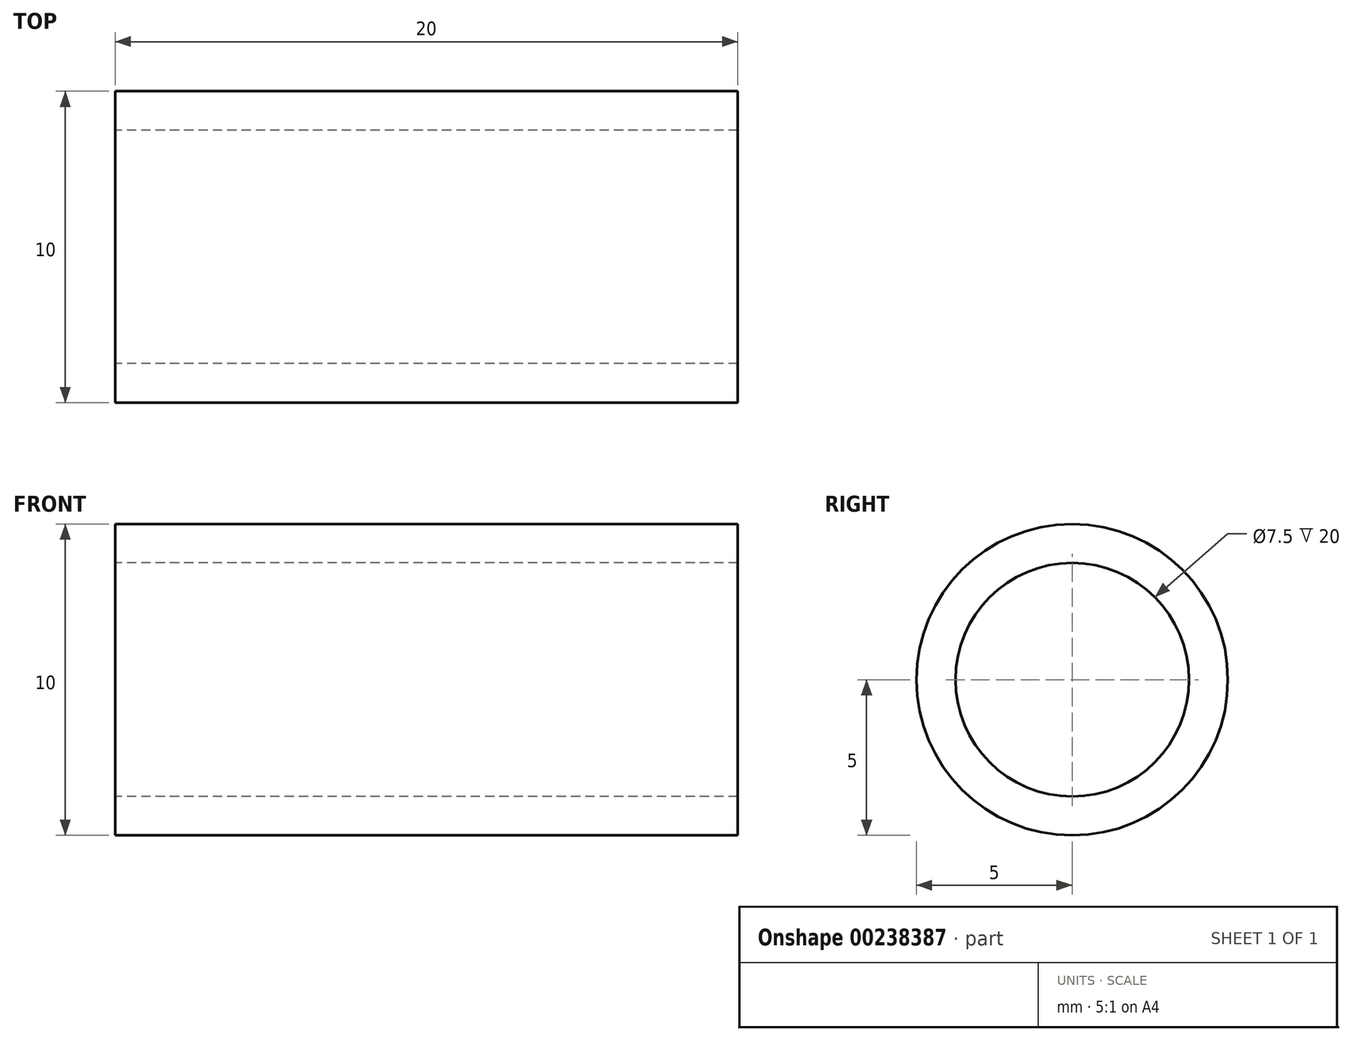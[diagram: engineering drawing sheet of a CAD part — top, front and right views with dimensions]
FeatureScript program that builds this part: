
annotation { "Feature Type Name" : "Feature", "Feature Type Description" : "" }
export const myFeature = defineFeature(function(context is Context, id is Id, definition is map)
    precondition{}
    {
        {
            var Q0;
            Q0=qCreatedBy(makeId("Right.planeOp"),FACE);
            var sketch = newSketch(context, id + "F0", { "sketchPlane" : qUnion([Q0])});
            skCircle(sketch, "E0", {"center": v(0, 0) * mm, "radius": 5 * mm});
            skCircle(sketch, "E1", {"center": v(0, 0) * mm, "radius": 3.75 * mm});
            skSolve(sketch);
        }
        {
            var Q0;
            Q0=makeQuery(id+"F0.imprint","IMPRINT",FACE,{"disambiguationData":[TD([[makeQuery(id+"F0.imprint","IMPRINT",EDGE,{"derivedFrom":sQuery(id+"F0.wireOp",EDGE,"E0")}),1.0]])]});
            extrude(context, id + "F1", {"entities" : qUnion([Q0]), "depth" : 20 * mm});
        }
    });
